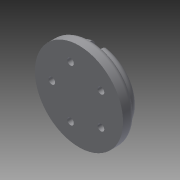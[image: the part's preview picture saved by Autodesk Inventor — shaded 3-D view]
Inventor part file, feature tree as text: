
AUTODESK INVENTOR PART (.ipt)
format: ipt  version: 2014 SP2 (Build 180246200, 246)  size: 170,496 bytes
history: native  units: mm
features: extrude x2, fillet x2, sketch x2
ambient origin geometry x8: Origin, YZ Plane, XZ Plane, XY Plane, X Axis, Y Axis, Z Axis, Center Point
bodies: Solid1 (feature_tree)
feature tree (6):
  extrude  "Extrusion1"  Depth=22.2mm
  extrude  "Extrusion2"  Depth=2.0mm
  fillet  "Fillet1"  Radius=2.7mm
  fillet  "Fillet2"  Radius=2.7mm
  sketch  "Sketch1"  dims[d0=36.0mm d1=22.2mm]
  sketch  "Sketch2"  dims[d2=2.7mm d3=2.7mm d4=2.7mm d5=2.7mm d6=2.7mm d7=5.0mm d8=0.0mm d9=30.0mm d11=2.5mm d14=4.0mm d15=0.0mm d16=2.5mm d17=5.0mm d18=5.0mm d19=0.0mm d20=2.5mm d21=2.0mm d22=2.0mm]
